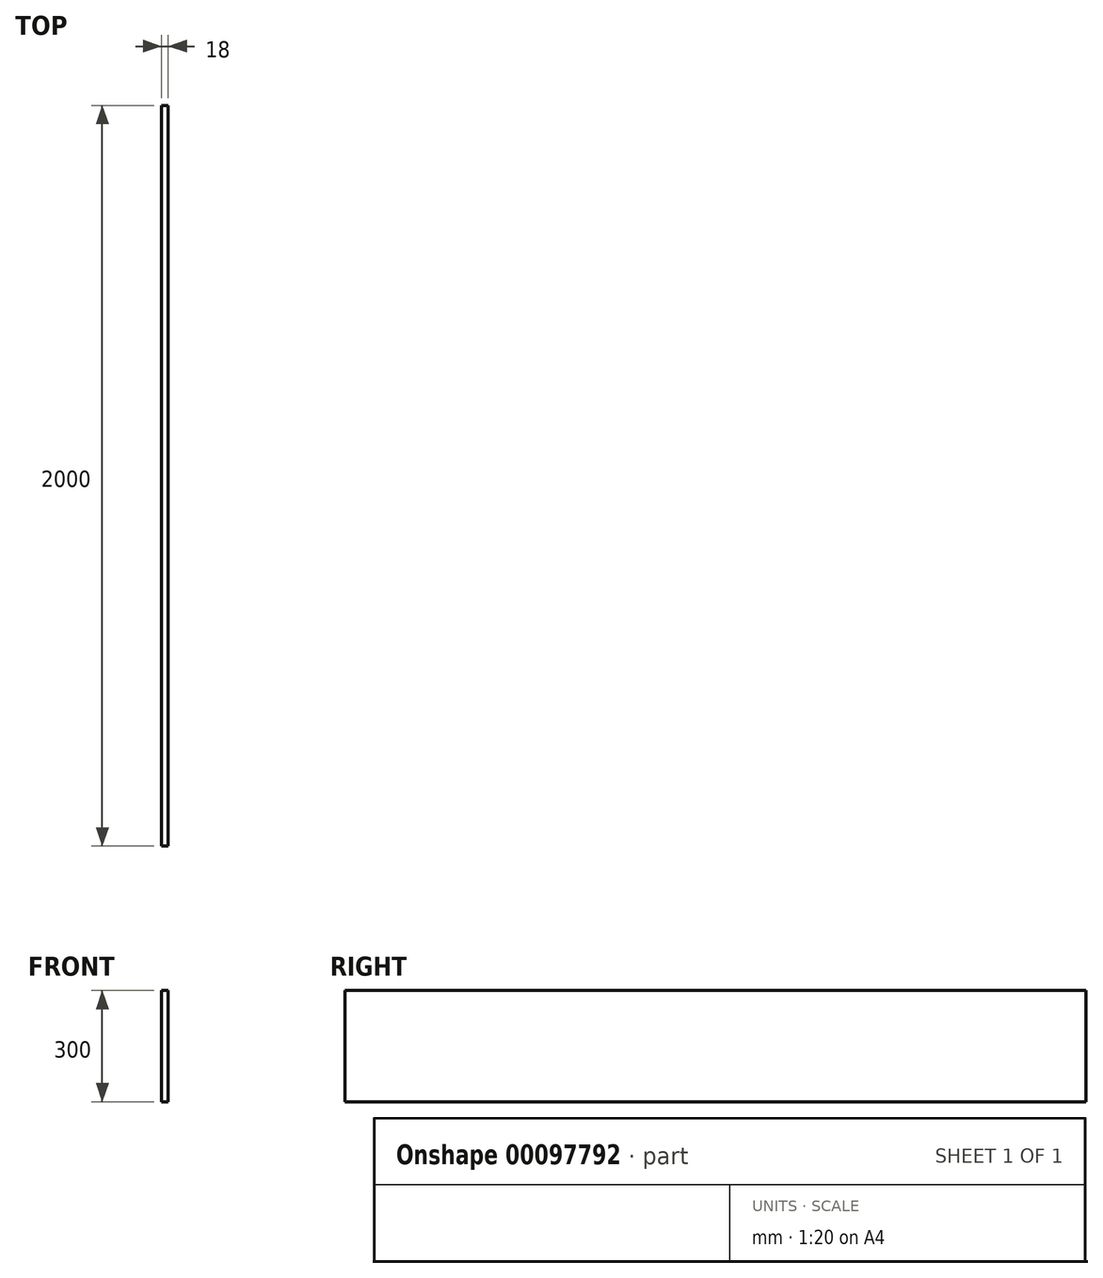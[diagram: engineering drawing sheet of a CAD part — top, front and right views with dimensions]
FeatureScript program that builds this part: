
annotation { "Feature Type Name" : "Feature", "Feature Type Description" : "" }
export const myFeature = defineFeature(function(context is Context, id is Id, definition is map)
    precondition{}
    {
        {
            var Q0;
            Q0=qCreatedBy(makeId("Front.planeOp"),FACE);
            var sketch = newSketch(context, id + "F0", { "sketchPlane" : qUnion([Q0])});
            skLineSegment(sketch, "E0.bottom", {"start": v(0, 0) * mm, "end": v(18, 0) * mm});
            skLineSegment(sketch, "E0.top", {"start": v(0, 300) * mm, "end": v(18, 300) * mm});
            skLineSegment(sketch, "E0.left", {"start": v(0, 0) * mm, "end": v(0, 300) * mm});
            skLineSegment(sketch, "E0.right", {"start": v(18, 0) * mm, "end": v(18, 300) * mm});
            skSolve(sketch);
        }
        {
            var Q0;
            Q0 = qSketchRegion(id + "F0", true);
            extrude(context, id + "F1", {"entities" : qUnion([Q0]), "oppositeDirection" : true, "depth" : 2000 * mm});
        }
    });
